# Revit family: QF_BPRO_BPT E 30 (24) x 1_1 C_575203
name_source: partatom
category: Sonderausstattung
revit_build: Autodesk Revit 2018 (Build: 20190510_1515(x64)
units: mm (PartAtom-declared; Revit-internal decimal feet)

## family parameters
Arbeitsebenenbasiert = Nein
Beim Laden mit Abzugskörper schneiden = Nein
Bemaßung runder Anschluss = Durchmesser verwenden
Gemeinsam genutzt = Nein
Immer vertikal = Ja
Raumberechnungspunkt = Nein
Teiletyp = Normal

## types (1)
- BPT E 30 (24) x 1/1 C
    Accessory = Ja
    Beschreibung = B.PROTHERM E 30 (24) x 1/1 cooled
B.PROTHERM E food transport container 1/1, convection-cooled,
made of corrosion-resistant steel, with hinged door, mobile.
30 support ledges: 24 x 1/1 and 6 x 1/2.
Space between ledges: 38.3 mm
Temperature range adjustable between +2 °C and +10 °C.
Refrigerant: propane R290
Mains frequency: 50/60 Hz
    CE Approved = Ja
    Conn Conduit = Ja
    Conn Plug = Schuko plug
    Cycle = 60 Hz
    Depth Actual = 821 mm
    Doorbar Height = 805 mm
    Foodservice Equipment Identifier = Ja
    Height Actual = 1532 mm
    Height Cooling = 1140 mm
    Height Wheels = 162 mm
    Hersteller = B.PRO GmbH
    Item Number = 575203
    Kosten = 6940 $
    Length Actual = 590 mm
    Main switch integrated = Ja
    Masterspec = Dimensions

Length:				  590 mm
Width:			  821 mm
Height:			1532 mm


Design

Design
The B.PROTHERM is made of AISI 304 stainless steel. The surface is micro-polished.  
The body and the hinged door are double-walled and fitted with CFC-free PUR foam panels 
to provide thermal insulation. The B.PROTHERM is mobile thanks to corrosion-resistant synthetic castors as per DIN 18867, Part 8 (2 fixed and 2 steering castors with brake, castor diameter 125 mm). The sturdy, synthetic base structure with integrated all-round bumper rail protects the unit and furniture from damage.

Body
The BPT E 30 (24) C's enclosed roof cover features stacking nubs, meaning B.PROTHERM synthetic containers can be stacked on it. The base and rear and side walls are fitted with all-round edge radius R2 and are spot-welded at their points of contact (hygienic type HS). The interior is fully equipped with 30 pairs of deep-drawn stainless steel ledge walls for easy cleaning and maximum hygiene. The support ledges have a uniform spacing of 38.3 mm to hold Gastronorm containers. This means all common spacing dimensions (about 75 mm, 115 mm) can be housed in a single unit and ensures efficient use of the interior. The support ledges in front of the refrigeration compartment can also be used thanks to the intelligent positioning of the refrigeration compartment on the rear panel in the lower interior. This means that 24 pairs of support ledges are provided to hold size GN 1/1 or its subdivisions and 
6 pairs of support ledges are provided to hold size GN 1/2 or its subdivisions.


 
On the rear panel of the interior body, an air baffle ensures optimum, rapid, uniform air circulation throughout the interior and also serves as a stop for inserted GN containers. Interior and exterior body are vertically connected with synthetic profiles and thermally separated.

The B.PROTHERM is equipped with 4 vertical push handles as standard to ensure optimum handling on all sides. The ergonomic length of the handles makes the trolley easy to manoeuvre for any trolley size. The push handles are located within the bumper rail to prevent the hands from being crushed when rolling through doors and narrow corridors. The helix cord and plug holder are attached on the unit rear and also within the all-round bumper rail.  

The B.PRO control is integrated into the top of the unit, making it easy to use. It contains the unit on/off button, a menu button, a function button and an up/down button, e.g. to regulate the temperature in the interior precisely. 

Door
The trolley is equipped with a door on its front that can be opened 270° and features a lock on its bottom plate. The door is inside the bumper rail when open or closed and is thus protected from damage. The push handles are still accessible when the door is open. The robust door hinges are made of stainless steel investment casting. The hinge design eliminates risk of injury if a user should accidentally take hold of the hinge.
The door is also fitted with an all-round, food-safe seal (TPE) that closes against the trolley body and can be removed. The seal features a hollow-chamber profile, so it has insulating properties and energy losses are minimised.
The built-in door contact switch ensures that refrigeration switches off when the door is open. This prevents the evaporator from icing up and unnecessary energy loss. 

The door is fitted with a 2-point locking system. It is easy to open from the outside by simply pushing up the door handle. 
The B.PROTHERM has a push-button which glows in the dark in its interior. The patented panic opening can be identified if someone should get accidentally locked inside the interior and the door lock can be unlocked from the inside by pressing the button. 
What is known as the afterglow effect meets the requirements for safety-relevant components specified in ISO 16069. 

Active convection cooling
The refrigeration unit is located in the body interior, protected by its outer casing. The refrigeration unit takes in air at the unit rear with the air inlet protected from dirt ingress and splashed water by a ventilation grate and air filter. The air exhaust outlet is located on the unit's lower surface. The B.PROTHERM interior contains a finned evaporator and a fan, which distributes the cold air uniformly in the unit interior through the evaporator via the air baffle integrated in the rear panel.

The active convection cooling is suitable for keeping food cold at a maximum temperature between +2 °C and +10 °C, as required for hygiene reasons. 

Options

•	Can be customised with powder coating on body and doors in 12 colours
•	Digitisation/connectivity for digital hygiene, temperature and process management. Sensors in the unit can be used to control software solutions, among other things.
•	With extra socket outlet on rear panel: instead of a plug holder, additional socket featured for coupling additional units. 
•	Additional bumper rail on top surface made of solid synthetic 
•	Top surface with stainless steel railing on 3 sides
•	(Smooth) top surface with stainless steel railing on 4 sides
•	Draw bar and coupling made of stainless steel
•	Hygienic type H1
•	Door, lockable
•	Menu card holder on the front of the door to hold DIN A5 and DIN A6 menu cards
•	Kick latch, with convenient, foot-operated door opening
•	Stainless-steel castors, 125 mm in diameter, 
2 fixed and 2 steering castors with brakes 
•	Anti-static castors, 125 mm in diameter, 
2 fixed and 2 steering castors with brakes, 
corrosion-resistant as per DIN 18867-8, synthetic
•	Galvanised steel castors, 160 mm in diameter, 
2 fixed and 2 steering castors with brakes 
•	Galvanised steel castors with elastic tyres, 
160 mm in diameter, 2 fixed and 2 steering castors with brakes 
•	Stainless-steel castors, 160 mm in diameter, 
2 fixed and 2 steering castors with brakes 
•	Stainless-steel castors with elastic tyres, 
160 mm in diameter, 2 fixed and 2 steering castors with brakes 

Accessories

•	Eutectic plate -3 °C, synthetic 
(order no. 568 136)
•	Eutectic plate -12 °C, synthetic 
(order no. 573 332)
•	Slide-in frame to sub-divide GN containers
with max. depth 150 mm (order no. 564 352)
•	Variable GN support bars for inserting a variety of GN containers 
of sizes GN 1/4, GN 1/6, GN 1/9 into the slide-in frame (ST 3 order no. 550 650; ST 5 order no. 550 651)
•	BPT E menu card, DIN A6 (order no. 572 513) 
•	Special pen for marking BPT E menu cards 
(order no. 564 361)
•	Menu card box, synthetic (order no. 564 355)

Technical data

Material:	Stainless steel,
	synthetic
Insulating material:		PUR foam panels, CFC-free 
Weight:	100 kg
Capacities:	
•	GN containers:	  8 units GN 1/1-100
	12 units GN 1/1-65
	16+2 units GN 1/2-100
	24+3 units GN 1/2-65
Ledges:	30 deep-drawn support ledges: 24 x 1/1 and 6 x 
1/ 2 GN
	Space between ledges of 38.3 mm
Temperature range:	Can be regulated down to the degree from +2 °C to +10 °C at an ambient temperature between +15 °C and +38 °C
Refrigerant:	Propane R290
Refrigerating capacity:	0.35 kW at t0= -10 °C and 
tu= +32 °C 
Climate class: 	4
Protection type: 	IPX5
Connected load:	220-240 V AC/50-60 Hz/
0.27 kW 
Emissions:	The workplace-specific noise 
	level for the unit is less than 
	70 dB(A) 


Special features

•	Extremely efficient, flexible use of interior thanks to uniform space between ledges of 38.3 mm
•	Active convection cooling with sophisticated airflow concept for rapid, uniform cooling distribution
•	12 different body colours, perfect for logistical coding and customisation
•	Environmentally friendly refrigerant propane R290 - natural, resource-saving and future-proof
•	Connectivity for digital hygiene, temperature and process management. You can digitalise all processes using the optionally integrable sensors to ensure safety and save time.

Make

Manufacturer:			B.PRO
Model:	BPT E 30 (24) C
	B.PROTHERM
Order no.			575 203
    Material = QF_Metal-Stainless-Steel_general
    Model Warning = Upright transport position:
Transport the unit in an upright position only. If the unit was not transported upright, wait 2 hours before commissioning.

Transport with a truck or delivery vehicle:
The unit may only be transported in a truck or delivery vehicle which features a loading ramp.
The loading ramp must not exceed an angle of inclination of 10°.

The unit is not properly secured for transport if only the castor brakes have been applied.
Secure the unit on all four sides to prevent it from shifting.
Secure the unit against vertical movement during transport.
Use padded locking bars. 

Location:
Never operate the unit next to equipment which emits large amounts of steam, such as a dishwasher.
Steam can cause moisture condensation on the unit.
When the unit is connected to the power, there is a danger of the moisture film causing a
short-circuit or an electric shock.

Keep the ventilation slits clear.
Ventilation slits must be at least 10 cm from a wall when the refrigeration unit is switched on.
Blocked ventilation slits can cause the refrigeration unit to overheat and fail.

Loading:
To prevent extension of the centre of gravity to the unit top, load unit from the bottom up when
loading partially.

Detailed safety information can be found in the operating instructions.
    Modell = BPT E 30 (24) x 1/1 C
    Sound Level = < 70 dB(A)
    Specification by Manufacturer = Dimensions

Length:				  590 mm
Width:			  821 mm
Height:			1532 mm


Design

Design
The B.PROTHERM is made of AISI 304 stainless steel. The surface is micro-polished.  
The body and the hinged door are double-walled and fitted with CFC-free PUR foam panels 
to provide thermal insulation. The B.PROTHERM is mobile thanks to corrosion-resistant synthetic castors as per DIN 18867, Part 8 (2 fixed and 2 steering castors with brake, castor diameter 125 mm). The sturdy, synthetic base structure with integrated all-round bumper rail protects the unit and furniture from damage.

Body
The BPT E 30 (24) C's enclosed roof cover features stacking nubs, meaning B.PROTHERM synthetic containers can be stacked on it. The base and rear and side walls are fitted with all-round edge radius R2 and are spot-welded at their points of contact (hygienic type HS). The interior is fully equipped with 30 pairs of deep-drawn stainless steel ledge walls for easy cleaning and maximum hygiene. The support ledges have a uniform spacing of 38.3 mm to hold Gastronorm containers. This means all common spacing dimensions (about 75 mm, 115 mm) can be housed in a single unit and ensures efficient use of the interior. The support ledges in front of the refrigeration compartment can also be used thanks to the intelligent positioning of the refrigeration compartment on the rear panel in the lower interior. This means that 24 pairs of support ledges are provided to hold size GN 1/1 or its subdivisions and 
6 pairs of support ledges are provided to hold size GN 1/2 or its subdivisions.


 
On the rear panel of the interior body, an air baffle ensures optimum, rapid, uniform air circulation throughout the interior and also serves as a stop for inserted GN containers. Interior and exterior body are vertically connected with synthetic profiles and thermally separated.

The B.PROTHERM is equipped with 4 vertical push handles as standard to ensure optimum handling on all sides. The ergonomic length of the handles makes the trolley easy to manoeuvre for any trolley size. The push handles are located within the bumper rail to prevent the hands from being crushed when rolling through doors and narrow corridors. The helix cord and plug holder are attached on the unit rear and also within the all-round bumper rail.  

The B.PRO control is integrated into the top of the unit, making it easy to use. It contains the unit on/off button, a menu button, a function button and an up/down button, e.g. to regulate the temperature in the interior precisely. 

Door
The trolley is equipped with a door on its front that can be opened 270° and features a lock on its bottom plate. The door is inside the bumper rail when open or closed and is thus protected from damage. The push handles are still accessible when the door is open. The robust door hinges are made of stainless steel investment casting. The hinge design eliminates risk of injury if a user should accidentally take hold of the hinge.
The door is also fitted with an all-round, food-safe seal (TPE) that closes against the trolley body and can be removed. The seal features a hollow-chamber profile, so it has insulating properties and energy losses are minimised.
The built-in door contact switch ensures that refrigeration switches off when the door is open. This prevents the evaporator from icing up and unnecessary energy loss. 

The door is fitted with a 2-point locking system. It is easy to open from the outside by simply pushing up the door handle. 
The B.PROTHERM has a push-button which glows in the dark in its interior. The patented panic opening can be identified if someone should get accidentally locked inside the interior and the door lock can be unlocked from the inside by pressing the button. 
What is known as the afterglow effect meets the requirements for safety-relevant components specified in ISO 16069. 

Active convection cooling
The refrigeration unit is located in the body interior, protected by its outer casing. The refrigeration unit takes in air at the unit rear with the air inlet protected from dirt ingress and splashed water by a ventilation grate and air filter. The air exhaust outlet is located on the unit's lower surface. The B.PROTHERM interior contains a finned evaporator and a fan, which distributes the cold air uniformly in the unit interior through the evaporator via the air baffle integrated in the rear panel.

The active convection cooling is suitable for keeping food cold at a maximum temperature between +2 °C and +10 °C, as required for hygiene reasons. 

Options

•	Can be customised with powder coating on body and doors in 12 colours
•	Digitisation/connectivity for digital hygiene, temperature and process management. Sensors in the unit can be used to control software solutions, among other things.
•	With extra socket outlet on rear panel: instead of a plug holder, additional socket featured for coupling additional units. 
•	Additional bumper rail on top surface made of solid synthetic 
•	Top surface with stainless steel railing on 3 sides
•	(Smooth) top surface with stainless steel railing on 4 sides
•	Draw bar and coupling made of stainless steel
•	Hygienic type H1
•	Door, lockable
•	Menu card holder on the front of the door to hold DIN A5 and DIN A6 menu cards
•	Kick latch, with convenient, foot-operated door opening
•	Stainless-steel castors, 125 mm in diameter, 
2 fixed and 2 steering castors with brakes 
•	Anti-static castors, 125 mm in diameter, 
2 fixed and 2 steering castors with brakes, 
corrosion-resistant as per DIN 18867-8, synthetic
•	Galvanised steel castors, 160 mm in diameter, 
2 fixed and 2 steering castors with brakes 
•	Galvanised steel castors with elastic tyres, 
160 mm in diameter, 2 fixed and 2 steering castors with brakes 
•	Stainless-steel castors, 160 mm in diameter, 
2 fixed and 2 steering castors with brakes 
•	Stainless-steel castors with elastic tyres, 
160 mm in diameter, 2 fixed and 2 steering castors with brakes 

Accessories

•	Eutectic plate -3 °C, synthetic 
(order no. 568 136)
•	Eutectic plate -12 °C, synthetic 
(order no. 573 332)
•	Slide-in frame to sub-divide GN containers
with max. depth 150 mm (order no. 564 352)
•	Variable GN support bars for inserting a variety of GN containers 
of sizes GN 1/4, GN 1/6, GN 1/9 into the slide-in frame (ST 3 order no. 550 650; ST 5 order no. 550 651)
•	BPT E menu card, DIN A6 (order no. 572 513) 
•	Special pen for marking BPT E menu cards 
(order no. 564 361)
•	Menu card box, synthetic (order no. 564 355)

Technical data

Material:	Stainless steel,
	synthetic
Insulating material:		PUR foam panels, CFC-free 
Weight:	100 kg
Capacities:	
•	GN containers:	  8 units GN 1/1-100
	12 units GN 1/1-65
	16+2 units GN 1/2-100
	24+3 units GN 1/2-65
Ledges:	30 deep-drawn support ledges: 24 x 1/1 and 6 x 
1/ 2 GN
	Space between ledges of 38.3 mm
Temperature range:	Can be regulated down to the degree from +2 °C to +10 °C at an ambient temperature between +15 °C and +38 °C
Refrigerant:	Propane R290
Refrigerating capacity:	0.35 kW at t0= -10 °C and 
tu= +32 °C 
Climate class: 	4
Protection type: 	IPX5
Connected load:	220-240 V AC/50-60 Hz/
0.27 kW 
Emissions:	The workplace-specific noise 
	level for the unit is less than 
	70 dB(A) 


Special features

•	Extremely efficient, flexible use of interior thanks to uniform space between ledges of 38.3 mm
•	Active convection cooling with sophisticated airflow concept for rapid, uniform cooling distribution
•	12 different body colours, perfect for logistical coding and customisation
•	Environmentally friendly refrigerant propane R290 - natural, resource-saving and future-proof
•	Connectivity for digital hygiene, temperature and process management. You can digitalise all processes using the optionally integrable sensors to ensure safety and save time.

Make

Manufacturer:			B.PRO
Model:	BPT E 30 (24) C
	B.PROTHERM
Order no.			575 203
    Typenkommentare = food transport container, convection-cooled
    URL = https://www.bpro-solutions.com
    URL Manufacturer = https://www.bpro-solutions.com
    URL Recommended Spares List = https://www.bpro-solutions.com
    Volts = 230 V
    Watts = 270 W
    Weight = 100.00 kg
    Width2 = 393 mm  [stored 1.28937 ft]

note: [stored X ft] marks values corroborated as IEEE doubles in the binary element streams (Revit-internal decimal feet)
